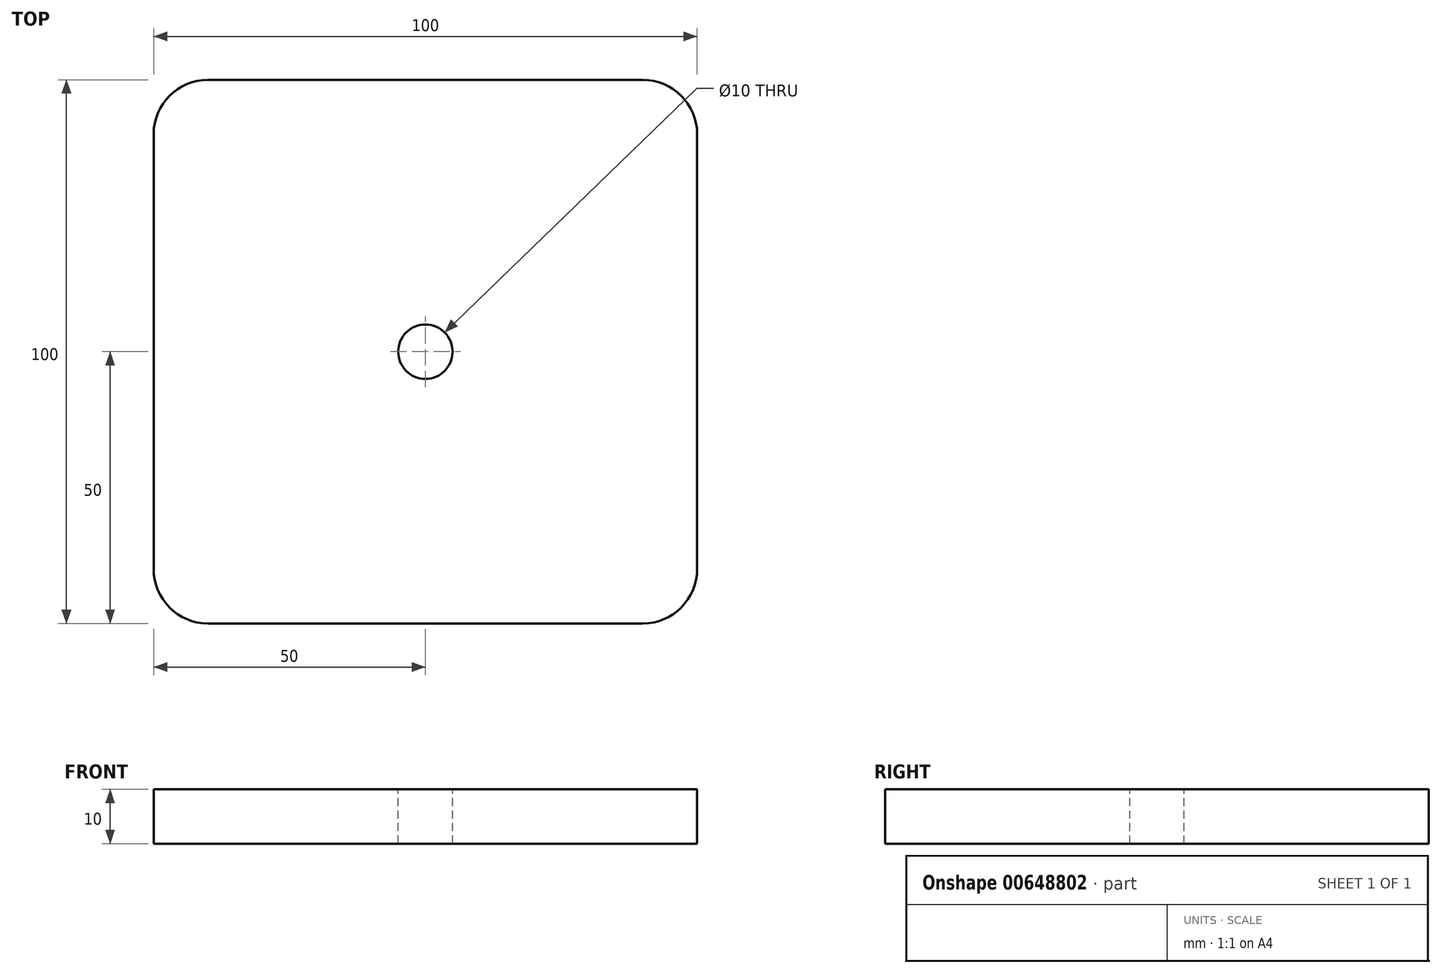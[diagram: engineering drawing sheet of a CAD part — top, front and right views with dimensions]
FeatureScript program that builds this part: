
annotation { "Feature Type Name" : "Feature", "Feature Type Description" : "" }
export const myFeature = defineFeature(function(context is Context, id is Id, definition is map)
    precondition{}
    {
        {
            var Q0;
            Q0=qCreatedBy(makeId("Top.planeOp"),FACE);
            var sketch = newSketch(context, id + "F0", { "sketchPlane" : qUnion([Q0])});
            skLineSegment(sketch, "E0.bottom", {"start": v(50, -50) * mm, "end": v(-50, -50) * mm});
            skLineSegment(sketch, "E0.top", {"start": v(50, 50) * mm, "end": v(-50, 50) * mm});
            skLineSegment(sketch, "E0.left", {"start": v(50, -50) * mm, "end": v(50, 50) * mm});
            skLineSegment(sketch, "E0.right", {"start": v(-50, -50) * mm, "end": v(-50, 50) * mm});
            skPoint(sketch, "E0.middle", {"position": v(0, 0) * mm});
            skSolve(sketch);
        }
        {
            var Q0;
            Q0=makeQuery(id+"F0.imprint","IMPRINT",FACE,{"disambiguationData":[TD([[makeQuery(id+"F0.imprint","IMPRINT",EDGE,{"derivedFrom":sQuery(id+"F0.wireOp",EDGE,"E0.bottom")}),-1.0]])]});
            extrude(context, id + "F1", {"entities" : qUnion([Q0]), "depth" : 10 * mm, "offsetDistance" : 25 * mm});
        }
        {
            var Q0;
            Q0=makeQuery(id+"F1.opExtrude","SWEPT_EDGE",EDGE,{"disambiguationData":[OSD([sQuery(id+"F0.wireOp",EDGE,"E0.bottom"),sQuery(id+"F0.wireOp",EDGE,"E0.right")])]});
            var Q1;
            Q1=makeQuery(id+"F1.opExtrude","SWEPT_EDGE",EDGE,{"disambiguationData":[OSD([sQuery(id+"F0.wireOp",EDGE,"E0.bottom"),sQuery(id+"F0.wireOp",EDGE,"E0.left")])]});
            var Q2;
            Q2=makeQuery(id+"F1.opExtrude","SWEPT_EDGE",EDGE,{"disambiguationData":[OSD([sQuery(id+"F0.wireOp",EDGE,"E0.top"),sQuery(id+"F0.wireOp",EDGE,"E0.left")])]});
            var Q3;
            Q3=makeQuery(id+"F1.opExtrude","SWEPT_EDGE",EDGE,{"disambiguationData":[OSD([sQuery(id+"F0.wireOp",EDGE,"E0.top"),sQuery(id+"F0.wireOp",EDGE,"E0.right")])]});
            fillet(context, id + "F2", {"entities" : qUnion([Q0, Q1, Q2, Q3]), "radius" : 10 * mm, "tangentPropagation" : true, "allowEdgeOverflow" : false});
        }
        {
            var Q0;
            Q0=sQuery(id+"F0.wireOp",VERTEX,"E0.middle");
            var Q1;
            Q1=makeQuery(id+"F1.opExtrude","SWEPT_BODY",BODY,{"disambiguationData":[OSD([sQuery(id+"F0.wireOp",EDGE,"E0.bottom"),sQuery(id+"F0.wireOp",EDGE,"E0.top"),sQuery(id+"F0.wireOp",EDGE,"E0.left"),sQuery(id+"F0.wireOp",EDGE,"E0.right")])]});
            hole(context, id + "F3", {"style" : HoleStyle.SIMPLE, "endStyle" : HoleEndStyle.THROUGH, "oppositeDirection" : true, "holeDiameter" : 10 * mm, "majorDiameter" : 5 * mm, "isTappedThrough" : true, "tappedDepth" : 12 * mm, "tapClearance" : 3, "locations" : qUnion([Q0]), "scope" : qUnion([Q1])});
        }
    });
